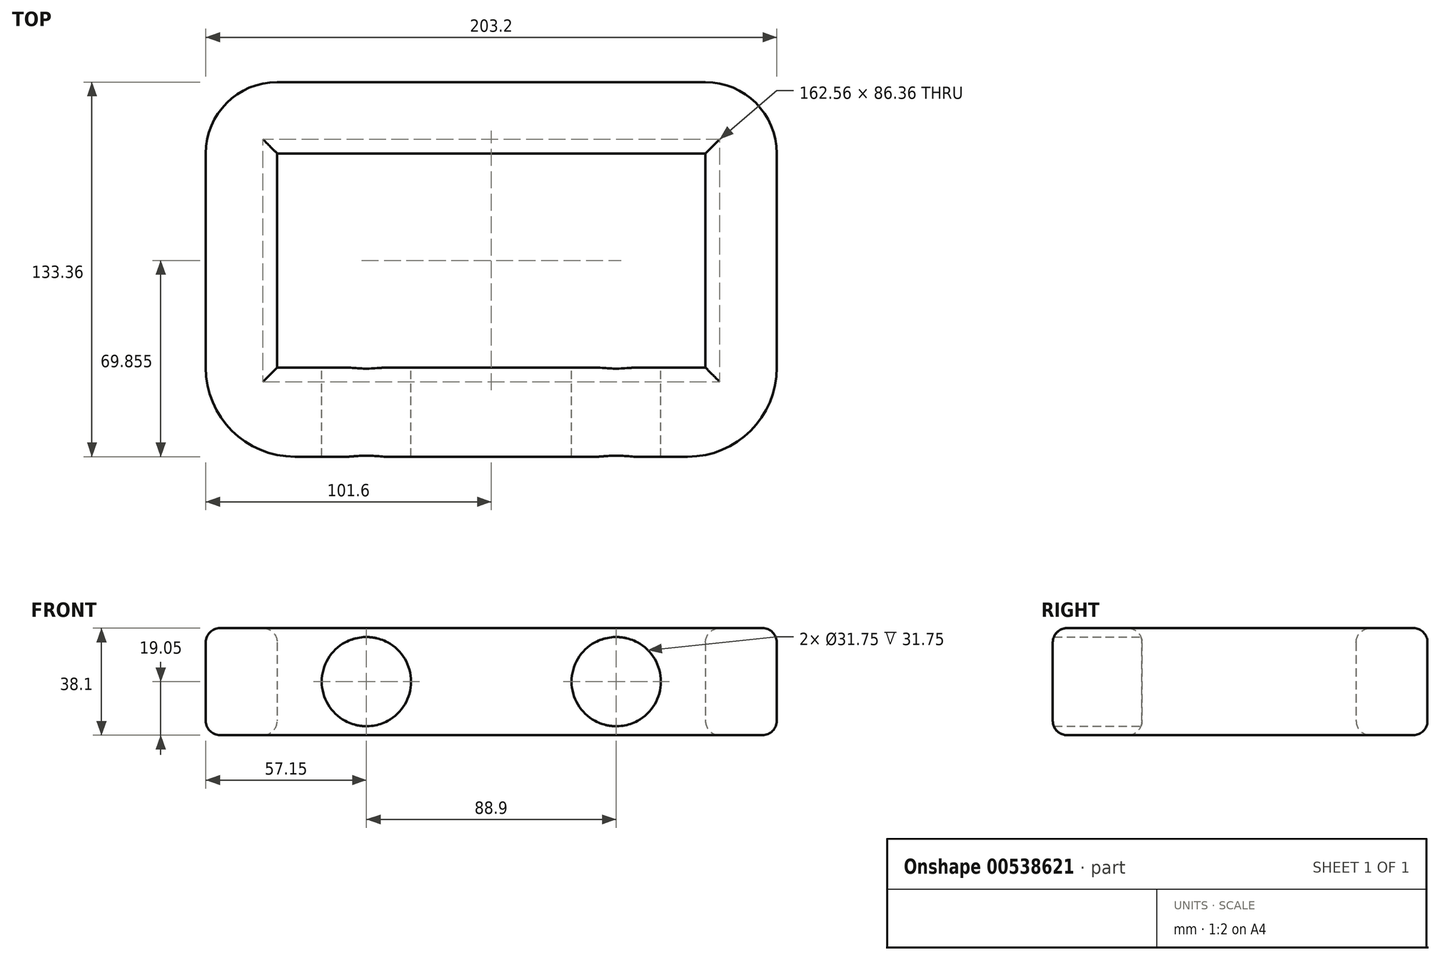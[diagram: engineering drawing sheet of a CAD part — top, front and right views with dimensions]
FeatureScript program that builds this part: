
annotation { "Feature Type Name" : "Feature", "Feature Type Description" : "" }
export const myFeature = defineFeature(function(context is Context, id is Id, definition is map)
    precondition{}
    {
        {
            var Q0;
            Q0=qCreatedBy(makeId("Front.planeOp"),FACE);
            var sketch = newSketch(context, id + "F0", { "sketchPlane" : qUnion([Q0])});
            skLineSegment(sketch, "E0.bottom", {"start": v(69.85, -19.05) * mm, "end": v(-69.85, -19.05) * mm});
            skLineSegment(sketch, "E0.top", {"start": v(69.85, 19.05) * mm, "end": v(-69.85, 19.05) * mm});
            skLineSegment(sketch, "E0.left", {"start": v(69.85, -19.05) * mm, "end": v(69.85, 19.05) * mm});
            skLineSegment(sketch, "E0.right", {"start": v(-69.85, -19.05) * mm, "end": v(-69.85, 19.05) * mm});
            skPoint(sketch, "E0.middle", {"position": v(0, 0) * mm});
            skCircle(sketch, "E1", {"center": v(-44.45, 0) * mm, "radius": 15.88 * mm});
            skCircle(sketch, "E2", {"center": v(44.45, 0) * mm, "radius": 15.88 * mm});
            skLineSegment(sketch, "E3", {"start": v(-44.45, 0) * mm, "end": v(0, 0) * mm, "construction": true});
            skLineSegment(sketch, "E4", {"start": v(0, 0) * mm, "end": v(44.45, 0) * mm, "construction": true});
            skSolve(sketch);
        }
        {
            var Q0;
            Q0=makeQuery(id+"F0.imprint","IMPRINT",FACE,{"disambiguationData":[TD([[makeQuery(id+"F0.imprint","IMPRINT",EDGE,{"derivedFrom":sQuery(id+"F0.wireOp",EDGE,"E0.bottom")}),-1.0]])]});
            extrude(context, id + "F1", {"entities" : qUnion([Q0]), "endBound" : BoundingType.SYMMETRIC, "depth" : 31.75 * mm, "offsetDistance" : 25.4 * mm});
        }
        {
            var Q0;
            Q0=makeQuery(id+"F1.opExtrude","SWEPT_FACE",FACE,{"disambiguationData":[OSD([sQuery(id+"F0.wireOp",EDGE,"E0.right")])]});
            var sketch = newSketch(context, id + "F2", { "sketchPlane" : qUnion([Q0])});
            skLineSegment(sketch, "E5.bottom", {"start": v(15.88, -19.05) * mm, "end": v(-15.88, -19.05) * mm});
            skLineSegment(sketch, "E5.top", {"start": v(15.88, 19.05) * mm, "end": v(-15.88, 19.05) * mm});
            skLineSegment(sketch, "E5.left", {"start": v(15.88, -19.05) * mm, "end": v(15.88, 19.05) * mm});
            skLineSegment(sketch, "E5.right", {"start": v(-15.88, -19.05) * mm, "end": v(-15.88, 19.05) * mm});
            skPoint(sketch, "E5.middle", {"position": v(0, 0) * mm});
            skSolve(sketch);
        }
        {
            var Q0;
            Q0=makeQuery(id+"F2.imprint","IMPRINT",FACE,{"disambiguationData":[TD([[makeQuery(id+"F2.imprint","IMPRINT",EDGE,{"derivedFrom":sQuery(id+"F2.wireOp",EDGE,"E5.bottom")}),-1.0]])]});
            var Q1;
            Q1=sQuery(id+"F2.wireOp",EDGE,"E5.right");
            revolve(context, id + "F3", {"operationType" : NewBodyOperationType.ADD, "entities" : qUnion([Q0]), "axis" : qUnion([Q1]), "revolveType" : RevolveType.ONE_DIRECTION, "oppositeDirection" : true, "angle" : 90 * degree});
        }
        {
            var Q0;
            Q0=makeQuery(id+"F3.boolean.opBoolean","MERGE",FACE,{"derivedFrom":[makeQuery(id+"F1.opExtrude","CAP_FACE",FACE,{"disambiguationData":[OSD([sQuery(id+"F0.wireOp",EDGE,"E0.bottom"),sQuery(id+"F0.wireOp",EDGE,"E0.top"),sQuery(id+"F0.wireOp",EDGE,"E0.left"),sQuery(id+"F0.wireOp",EDGE,"E0.right"),sQuery(id+"F0.wireOp",EDGE,"E1"),sQuery(id+"F0.wireOp",EDGE,"E2")])],"isStart":true}),makeQuery(id+"F3.opRevolve","CAP_FACE",FACE,{"disambiguationData":[OSD([sQuery(id+"F2.wireOp",EDGE,"E5.bottom"),sQuery(id+"F2.wireOp",EDGE,"E5.top"),sQuery(id+"F2.wireOp",EDGE,"E5.left"),sQuery(id+"F2.wireOp",EDGE,"E5.right")])],"isStart":false})]});
            var sketch = newSketch(context, id + "F4", { "sketchPlane" : qUnion([Q0])});
            skLineSegment(sketch, "E6.bottom", {"start": v(101.6, 19.05) * mm, "end": v(76.2, 19.05) * mm});
            skLineSegment(sketch, "E6.top", {"start": v(101.6, -19.05) * mm, "end": v(76.2, -19.05) * mm});
            skLineSegment(sketch, "E6.left", {"start": v(101.6, 19.05) * mm, "end": v(101.6, -19.05) * mm});
            skLineSegment(sketch, "E6.right", {"start": v(76.2, 19.05) * mm, "end": v(76.2, -19.05) * mm});
            skSolve(sketch);
        }
        {
            var Q0;
            Q0=makeQuery(id+"F4.imprint","IMPRINT",FACE,{"disambiguationData":[TD([[makeQuery(id+"F4.imprint","IMPRINT",EDGE,{"derivedFrom":sQuery(id+"F4.wireOp",EDGE,"E6.bottom")}),-1.0]])]});
            extrude(context, id + "F5", {"entities" : qUnion([Q0]), "operationType" : NewBodyOperationType.ADD, "depth" : 76.2 * mm, "offsetDistance" : 25.4 * mm});
        }
        {
            var Q0;
            Q0=makeQuery(id+"F5.opExtrude","CAP_FACE",FACE,{"disambiguationData":[OSD([sQuery(id+"F4.wireOp",EDGE,"E6.bottom"),sQuery(id+"F4.wireOp",EDGE,"E6.top"),sQuery(id+"F4.wireOp",EDGE,"E6.left"),sQuery(id+"F4.wireOp",EDGE,"E6.right")])],"isStart":false});
            var Q1;
            Q1=makeQuery(id+"F5.opExtrude","CAP_EDGE",EDGE,{"disambiguationData":[OSD([sQuery(id+"F4.wireOp",EDGE,"E6.right")])],"isStart":false});
            revolve(context, id + "F6", {"operationType" : NewBodyOperationType.ADD, "entities" : qUnion([Q0]), "axis" : qUnion([Q1]), "revolveType" : RevolveType.ONE_DIRECTION, "angle" : 90 * degree});
        }
        {
            var Q0;
            {var subQ0=sQuery(id+"F4.wireOp",EDGE,"E6.right");Q0=makeQuery(id+"F6.boolean.opBoolean","MERGE",FACE,{"derivedFrom":[makeQuery(id+"F5.opExtrude","SWEPT_FACE",FACE,{"disambiguationData":[OSD([subQ0])]}),makeQuery(id+"F6.opRevolve","CAP_FACE",FACE,{"disambiguationData":[OSD([sQuery(id+"F4.wireOp",EDGE,"E6.bottom"),sQuery(id+"F4.wireOp",EDGE,"E6.top"),sQuery(id+"F4.wireOp",EDGE,"E6.left"),subQ0])],"isStart":false})]});}
            var sketch = newSketch(context, id + "F7", { "sketchPlane" : qUnion([Q0])});
            skLineSegment(sketch, "E7.bottom", {"start": v(117.47, 19.05) * mm, "end": v(92.07, 19.05) * mm});
            skLineSegment(sketch, "E7.top", {"start": v(117.47, -19.05) * mm, "end": v(92.07, -19.05) * mm});
            skLineSegment(sketch, "E7.left", {"start": v(117.47, 19.05) * mm, "end": v(117.47, -19.05) * mm});
            skLineSegment(sketch, "E7.right", {"start": v(92.07, 19.05) * mm, "end": v(92.07, -19.05) * mm});
            skSolve(sketch);
        }
        {
            var Q0;
            Q0=makeQuery(id+"F7.imprint","IMPRINT",FACE,{"disambiguationData":[TD([[makeQuery(id+"F7.imprint","IMPRINT",EDGE,{"derivedFrom":sQuery(id+"F7.wireOp",EDGE,"E7.bottom")}),1.0]])]});
            var Q1;
            Q1=qCreatedBy(makeId("Right.planeOp"),FACE);
            extrude(context, id + "F8", {"entities" : qUnion([Q0]), "operationType" : NewBodyOperationType.ADD, "endBound" : BoundingType.UP_TO_SURFACE, "depth" : 25.4 * mm, "endBoundEntityFace" : qUnion([Q1]), "offsetDistance" : 25.4 * mm});
        }
        {
            var Q0;
            Q0=makeQuery(id+"F1.opExtrude","SWEPT_FACE",FACE,{"disambiguationData":[OSD([sQuery(id+"F0.wireOp",EDGE,"E0.left")])]});
            var Q1;
            Q1=makeQuery(id+"F1.opExtrude","CAP_EDGE",EDGE,{"disambiguationData":[OSD([sQuery(id+"F0.wireOp",EDGE,"E0.left")])],"isStart":true});
            revolve(context, id + "F9", {"operationType" : NewBodyOperationType.ADD, "entities" : qUnion([Q0]), "axis" : qUnion([Q1]), "revolveType" : RevolveType.ONE_DIRECTION, "angle" : 90 * degree});
        }
        {
            var Q0;
            {var subQ0=sQuery(id+"F0.wireOp",EDGE,"E0.left");Q0=makeQuery(id+"F9.boolean.opBoolean","MERGE",FACE,{"derivedFrom":[makeQuery(id+"F3.boolean.opBoolean","MERGE",FACE,{"derivedFrom":[makeQuery(id+"F1.opExtrude","CAP_FACE",FACE,{"disambiguationData":[OSD([sQuery(id+"F0.wireOp",EDGE,"E0.bottom"),sQuery(id+"F0.wireOp",EDGE,"E0.top"),subQ0,sQuery(id+"F0.wireOp",EDGE,"E0.right"),sQuery(id+"F0.wireOp",EDGE,"E1"),sQuery(id+"F0.wireOp",EDGE,"E2")])],"isStart":true}),makeQuery(id+"F3.opRevolve","CAP_FACE",FACE,{"disambiguationData":[OSD([sQuery(id+"F2.wireOp",EDGE,"E5.bottom"),sQuery(id+"F2.wireOp",EDGE,"E5.top"),sQuery(id+"F2.wireOp",EDGE,"E5.left"),sQuery(id+"F2.wireOp",EDGE,"E5.right")])],"isStart":false})]}),makeQuery(id+"F9.opRevolve","CAP_FACE",FACE,{"disambiguationData":[OSD([subQ0])],"isStart":false})]});}
            var sketch = newSketch(context, id + "F10", { "sketchPlane" : qUnion([Q0])});
            skLineSegment(sketch, "E8.bottom", {"start": v(-101.6, 19.05) * mm, "end": v(-76.2, 19.05) * mm});
            skLineSegment(sketch, "E8.top", {"start": v(-101.6, -19.05) * mm, "end": v(-76.2, -19.05) * mm});
            skLineSegment(sketch, "E8.left", {"start": v(-101.6, 19.05) * mm, "end": v(-101.6, -19.05) * mm});
            skLineSegment(sketch, "E8.right", {"start": v(-76.2, 19.05) * mm, "end": v(-76.2, -19.05) * mm});
            skSolve(sketch);
        }
        {
            var Q0;
            Q0=makeQuery(id+"F10.imprint","IMPRINT",FACE,{"disambiguationData":[TD([[makeQuery(id+"F10.imprint","IMPRINT",EDGE,{"derivedFrom":sQuery(id+"F10.wireOp",EDGE,"E8.bottom")}),-1.0]])]});
            extrude(context, id + "F11", {"entities" : qUnion([Q0]), "operationType" : NewBodyOperationType.ADD, "depth" : 76.2 * mm, "offsetDistance" : 25.4 * mm});
        }
        {
            var Q0;
            Q0=makeQuery(id+"F11.opExtrude","CAP_FACE",FACE,{"disambiguationData":[OSD([sQuery(id+"F10.wireOp",EDGE,"E8.bottom"),sQuery(id+"F10.wireOp",EDGE,"E8.top"),sQuery(id+"F10.wireOp",EDGE,"E8.left"),sQuery(id+"F10.wireOp",EDGE,"E8.right")])],"isStart":false});
            var Q1;
            Q1=makeQuery(id+"F11.opExtrude","CAP_EDGE",EDGE,{"disambiguationData":[OSD([sQuery(id+"F10.wireOp",EDGE,"E8.right")])],"isStart":false});
            revolve(context, id + "F12", {"operationType" : NewBodyOperationType.ADD, "entities" : qUnion([Q0]), "axis" : qUnion([Q1]), "revolveType" : RevolveType.ONE_DIRECTION, "oppositeDirection" : true, "angle" : 90 * degree});
        }
        {
            var Q0;
            Q0=makeQuery(id+"F8.opExtrude","CAP_FACE",FACE,{"disambiguationData":[OSD([sQuery(id+"F7.wireOp",EDGE,"E7.bottom"),sQuery(id+"F7.wireOp",EDGE,"E7.top"),sQuery(id+"F7.wireOp",EDGE,"E7.left"),sQuery(id+"F7.wireOp",EDGE,"E7.right")])],"isStart":false});
            var Q1;
            {var subQ0=sQuery(id+"F10.wireOp",EDGE,"E8.right");Q1=makeQuery(id+"F12.boolean.opBoolean","MERGE",FACE,{"derivedFrom":[makeQuery(id+"F11.opExtrude","SWEPT_FACE",FACE,{"disambiguationData":[OSD([subQ0])]}),makeQuery(id+"F12.opRevolve","CAP_FACE",FACE,{"disambiguationData":[OSD([sQuery(id+"F10.wireOp",EDGE,"E8.bottom"),sQuery(id+"F10.wireOp",EDGE,"E8.top"),sQuery(id+"F10.wireOp",EDGE,"E8.left"),subQ0])],"isStart":false})]});}
            extrude(context, id + "F13", {"entities" : qUnion([Q0]), "operationType" : NewBodyOperationType.ADD, "endBound" : BoundingType.UP_TO_SURFACE, "depth" : 25.4 * mm, "endBoundEntityFace" : qUnion([Q1]), "offsetDistance" : 25.4 * mm});
        }
        {
            var Q0;
            {var subQ0=sQuery(id+"F7.wireOp",EDGE,"E7.bottom");var subQ1=sQuery(id+"F10.wireOp",EDGE,"E8.bottom");var subQ2=sQuery(id+"F0.wireOp",EDGE,"E0.top");var subQ3=sQuery(id+"F4.wireOp",EDGE,"E6.bottom");Q0=makeQuery(id+"F13.boolean.opBoolean","MERGE",FACE,{"derivedFrom":[makeQuery(id+"F12.boolean.opBoolean","MERGE",FACE,{"derivedFrom":[makeQuery(id+"F11.boolean.opBoolean","MERGE",FACE,{"derivedFrom":[makeQuery(id+"F9.boolean.opBoolean","MERGE",FACE,{"derivedFrom":[makeQuery(id+"F8.boolean.opBoolean","MERGE",FACE,{"derivedFrom":[makeQuery(id+"F6.boolean.opBoolean","MERGE",FACE,{"derivedFrom":[makeQuery(id+"F5.boolean.opBoolean","MERGE",FACE,{"derivedFrom":[makeQuery(id+"F3.boolean.opBoolean","MERGE",FACE,{"derivedFrom":[makeQuery(id+"F1.opExtrude","SWEPT_FACE",FACE,{"disambiguationData":[OSD([subQ2])]}),makeQuery(id+"F3.opRevolve","SWEPT_FACE",FACE,{"disambiguationData":[OSD([sQuery(id+"F2.wireOp",EDGE,"E5.top")])]})]}),makeQuery(id+"F5.opExtrude","SWEPT_FACE",FACE,{"disambiguationData":[OSD([subQ3])]})]}),makeQuery(id+"F6.opRevolve","SWEPT_FACE",FACE,{"disambiguationData":[OSD([subQ3])]})]}),makeQuery(id+"F8.opExtrude","SWEPT_FACE",FACE,{"disambiguationData":[OSD([subQ0])]})]}),makeQuery(id+"F9.opRevolve","SWEPT_FACE",FACE,{"disambiguationData":[OSD([subQ2,sQuery(id+"F0.wireOp",EDGE,"E0.left")])]})]}),makeQuery(id+"F11.opExtrude","SWEPT_FACE",FACE,{"disambiguationData":[OSD([subQ1])]})]}),makeQuery(id+"F12.opRevolve","SWEPT_FACE",FACE,{"disambiguationData":[OSD([subQ1])]})]}),makeQuery(id+"F13.opExtrude","SWEPT_FACE",FACE,{"disambiguationData":[OSD([subQ0])]})]});}
            var Q1;
            {var subQ0=sQuery(id+"F7.wireOp",EDGE,"E7.top");var subQ1=sQuery(id+"F10.wireOp",EDGE,"E8.top");var subQ2=sQuery(id+"F0.wireOp",EDGE,"E0.bottom");var subQ3=sQuery(id+"F4.wireOp",EDGE,"E6.top");Q1=makeQuery(id+"F13.boolean.opBoolean","MERGE",FACE,{"derivedFrom":[makeQuery(id+"F12.boolean.opBoolean","MERGE",FACE,{"derivedFrom":[makeQuery(id+"F11.boolean.opBoolean","MERGE",FACE,{"derivedFrom":[makeQuery(id+"F9.boolean.opBoolean","MERGE",FACE,{"derivedFrom":[makeQuery(id+"F8.boolean.opBoolean","MERGE",FACE,{"derivedFrom":[makeQuery(id+"F6.boolean.opBoolean","MERGE",FACE,{"derivedFrom":[makeQuery(id+"F5.boolean.opBoolean","MERGE",FACE,{"derivedFrom":[makeQuery(id+"F3.boolean.opBoolean","MERGE",FACE,{"derivedFrom":[makeQuery(id+"F1.opExtrude","SWEPT_FACE",FACE,{"disambiguationData":[OSD([subQ2])]}),makeQuery(id+"F3.opRevolve","SWEPT_FACE",FACE,{"disambiguationData":[OSD([sQuery(id+"F2.wireOp",EDGE,"E5.bottom")])]})]}),makeQuery(id+"F5.opExtrude","SWEPT_FACE",FACE,{"disambiguationData":[OSD([subQ3])]})]}),makeQuery(id+"F6.opRevolve","SWEPT_FACE",FACE,{"disambiguationData":[OSD([subQ3])]})]}),makeQuery(id+"F8.opExtrude","SWEPT_FACE",FACE,{"disambiguationData":[OSD([subQ0])]})]}),makeQuery(id+"F9.opRevolve","SWEPT_FACE",FACE,{"disambiguationData":[OSD([subQ2,sQuery(id+"F0.wireOp",EDGE,"E0.left")])]})]}),makeQuery(id+"F11.opExtrude","SWEPT_FACE",FACE,{"disambiguationData":[OSD([subQ1])]})]}),makeQuery(id+"F12.opRevolve","SWEPT_FACE",FACE,{"disambiguationData":[OSD([subQ1])]})]}),makeQuery(id+"F13.opExtrude","SWEPT_FACE",FACE,{"disambiguationData":[OSD([subQ0])]})]});}
            fillet(context, id + "F14", {"entities" : qUnion([Q0, Q1]), "radius" : 5.08 * mm, "tangentPropagation" : true, "allowEdgeOverflow" : false});
        }
    });
